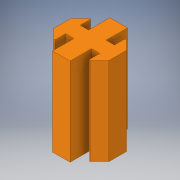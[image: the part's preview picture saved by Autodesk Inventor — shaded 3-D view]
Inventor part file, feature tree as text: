
AUTODESK INVENTOR PART (.ipt)
format: ipt  version: 2019 (Build 230136000, 136)  size: 140,800 bytes
history: native  units: in
note: dims shown in document units (in); Inventor stores cm internally (conversion verified against a paired STEP export)
features: extrude x1, fillet x1, sketch x1
ambient origin geometry x8: Origin, YZ Plane, XZ Plane, XY Plane, X Axis, Y Axis, Z Axis, Center Point
bodies: Body1 (feature_tree)
feature tree (3):
  extrude  "Extrusion2"  Depth=0.655in
  fillet  "Fillet1"  Radius=0.095in
  sketch  "Sketch1"  dims[d0=0.2in d1=0.655in d2=0.095in d4=0.1677in d9=0.121in d12=0.0in d15=0.442in d16=0.442in d20=135.0deg d21=135.0deg d24=0.2437in d25=0.655in d26=0.1372in d33=0.1372in d34=0.121in d35=0.095in d36=0.2437in d37=0.2in d38=0.2in d39=135.0deg d40=135.0deg d41=1.0in d42=0.0in d43=0.01in]
